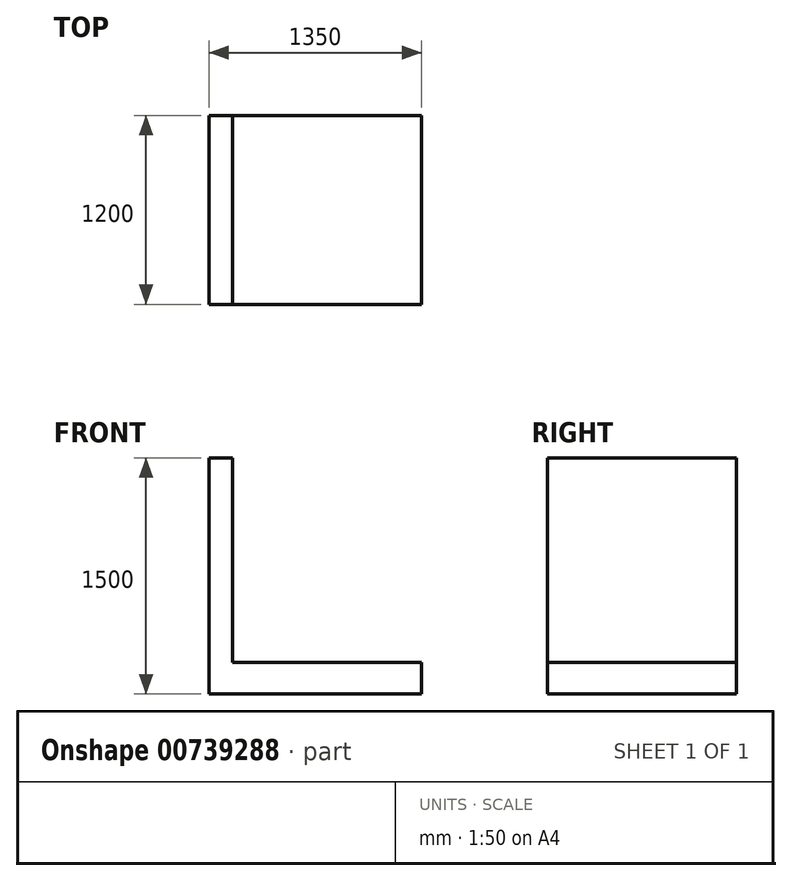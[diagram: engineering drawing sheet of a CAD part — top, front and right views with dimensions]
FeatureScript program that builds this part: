
annotation { "Feature Type Name" : "Feature", "Feature Type Description" : "" }
export const myFeature = defineFeature(function(context is Context, id is Id, definition is map)
    precondition{}
    {
        {
            var Q0;
            Q0=qCreatedBy(makeId("Top.planeOp"),FACE);
            var sketch = newSketch(context, id + "F0", { "sketchPlane" : qUnion([Q0])});
            skLineSegment(sketch, "E0.bottom", {"start": v(0, 0) * mm, "end": v(1200, 0) * mm});
            skLineSegment(sketch, "E0.top", {"start": v(0, 1200) * mm, "end": v(1200, 1200) * mm});
            skLineSegment(sketch, "E0.left", {"start": v(0, 0) * mm, "end": v(0, 1200) * mm});
            skLineSegment(sketch, "E0.right", {"start": v(1200, 0) * mm, "end": v(1200, 1200) * mm});
            skSolve(sketch);
        }
        {
            var Q0;
            Q0=makeQuery(id+"F0.imprint","IMPRINT",FACE,{"disambiguationData":[TD([[makeQuery(id+"F0.imprint","IMPRINT",EDGE,{"derivedFrom":sQuery(id+"F0.wireOp",EDGE,"E0.bottom")}),1.0]])]});
            extrude(context, id + "F1", {"entities" : qUnion([Q0]), "oppositeDirection" : true, "depth" : 200 * mm, "offsetDistance" : 25 * mm});
        }
        {
            var Q0;
            Q0=makeQuery(id+"F1.opExtrude","SWEPT_FACE",FACE,{"disambiguationData":[OSD([sQuery(id+"F0.wireOp",EDGE,"E0.bottom")])]});
            var sketch = newSketch(context, id + "F2", { "sketchPlane" : qUnion([Q0])});
            skLineSegment(sketch, "E1.bottom", {"start": v(0, -200) * mm, "end": v(-150, -200) * mm});
            skLineSegment(sketch, "E1.top", {"start": v(0, 1300) * mm, "end": v(-150, 1300) * mm});
            skLineSegment(sketch, "E1.left", {"start": v(0, -200) * mm, "end": v(0, 1300) * mm});
            skLineSegment(sketch, "E1.right", {"start": v(-150, -200) * mm, "end": v(-150, 1300) * mm});
            skSolve(sketch);
        }
        {
            var Q0;
            {var subQ3=sQuery(id+"F2.wireOp",EDGE,"E1.bottom");Q0=makeQuery(id+"F2.imprint","IMPRINT",FACE,{"disambiguationData":[TD([[makeQuery(id+"F2.imprint","IMPRINT",EDGE,{"derivedFrom":subQ3}),-1.0]])]});}
            extrude(context, id + "F3", {"entities" : qUnion([Q0]), "operationType" : NewBodyOperationType.ADD, "oppositeDirection" : true, "depth" : 1200 * mm, "offsetDistance" : 25 * mm});
        }
    });
